# Revit family: BE_66411_de_DE
name_source: partatom
category: Leuchten
revit_build: Autodesk Revit 2015 (Build: 20150704_0715(x64)
units: mm (PartAtom-declared; Revit-internal decimal feet)

## types (4) — shared parameters
AC/DC = AC/DC
Aktualisierung = 2015-10-30T08:54:00
BEGA_Dummy = Nein
BEGA_IES = Ja
BEGA_Intern = Ja
BEGA_Intern_Konstruktion = Ja
BEGA_Intern_an = Ja
BEGA_Intern_aus = Ja
Befestigungsabstand = 70 mm
Befestigungsbohrung = Ø 5,2 mm
Beschreibung = Wandleuchte
Beschreibung_Sonderanfertigung = Hier können Sie Informationen zur Sonderanfertigung eintragen.
CE_Konformität = ja
Energieeffizienzklasse = LED A++ - A
Farbfilter = 16777215
Farbtemperaturverschiebung bei Dämpfen der Lampe = <Keine Auswahl>
Farbwiedergabeindex = Ra > 80
Frequenz = 0/50-60 Hz
Gewicht = 1.8 kg
Hersteller = BEGA
Lampe = LED 10.5 W
Lastklassifizierung = Beleuchtung
Lebensdauerkriterien = L70 = 50.000 h
Leuchtenlichtstrom = 677 lm
Logo = BEGA_Logo.png
Material_03 = BEGA_Oberfläche_Weiss_matt
Material_11 = BEGA_Glas_opal
Neigungswinkel = 0.00°
Produktdatenblatt = http://www.bega.de
Scheinlast = 0 VA
Schutzart = IP 44
Schutzklasse = I
Sonderanfertigung = Nein
Spannung = 0 V
Typenbild = 66411.png
URL = http://www.bega.de
zero-valued in all types: Vorgabe-Ansicht

## per-type parameters (varying)
| type | Bestellnummer | Datei für fotometrisches Netz | Farbtemperatur | LED_Modulbezeichnung | Lampenlichtstrom | M_G | M_W | Modell |
| BEGA_66411_Grafit_K4 | 66411K4 | BE_66411K4.IES | 4000 K | LED-0505/840 | 1320 lm | Ja | Nein | 66411K4 |
| BEGA_66411_Weiß_K3 | 66411W | BE_66411.IES | 3000 K | LED-0505/830 | 1230 lm | Nein | Ja | 66411W |
| BEGA_66411_Weiß_K4 | 66411WK4 | BE_66411K4.IES | 4000 K | LED-0505/840 | 1320 lm | Nein | Ja | 66411WK4 |
| BEGA_66411_Grafit_K3 | 66411 | BE_66411.IES | 3000 K | LED-0505/830 | 1230 lm | Ja | Nein | 66411 |
